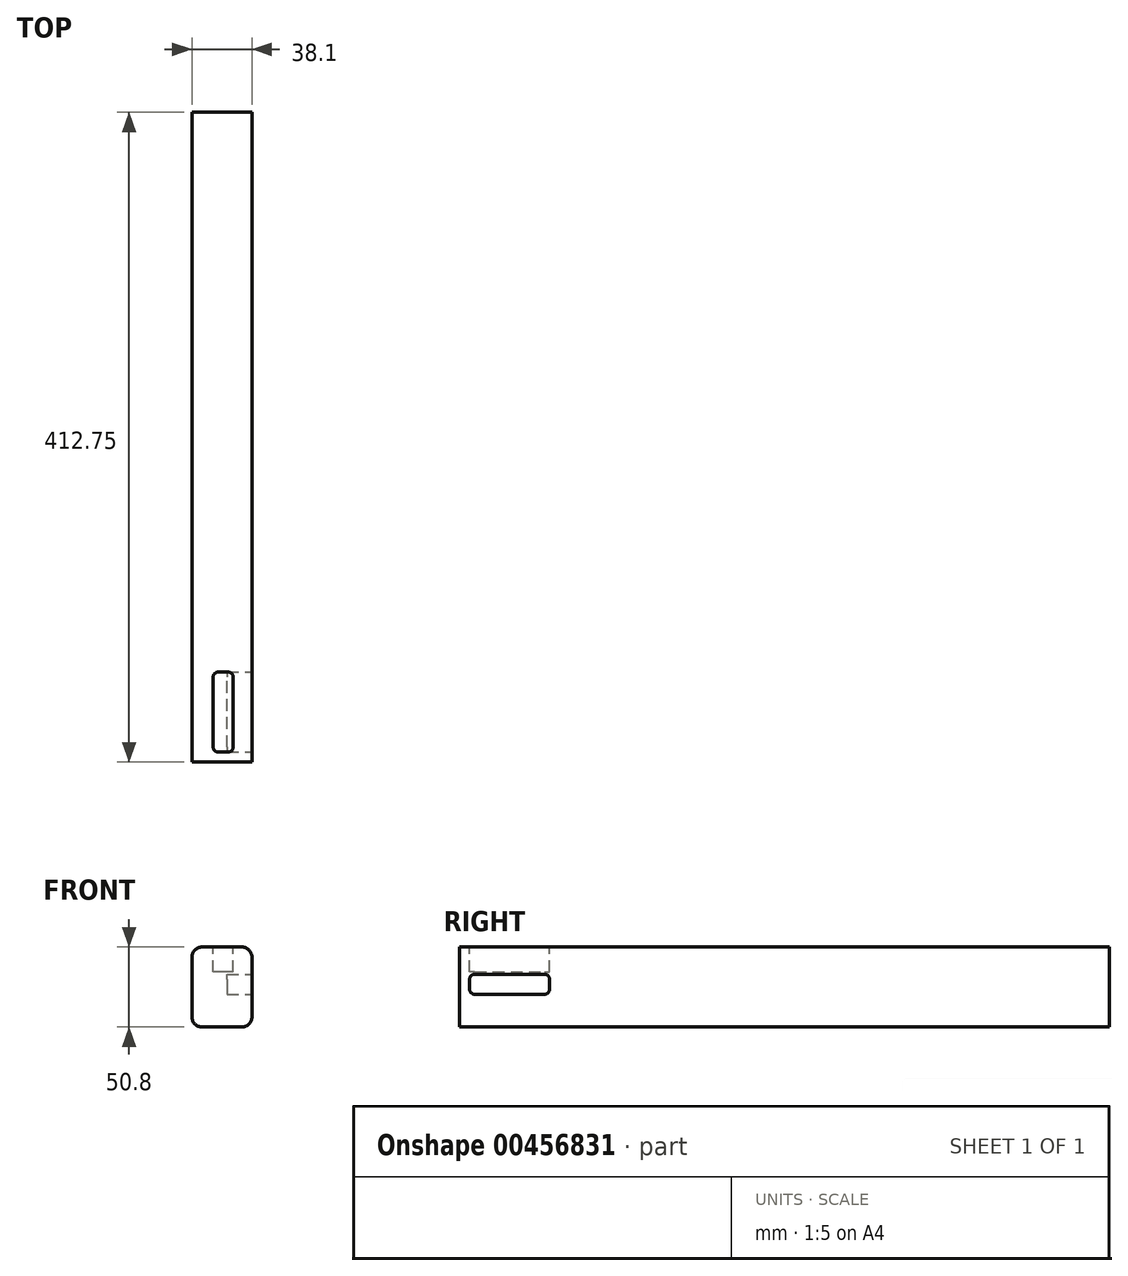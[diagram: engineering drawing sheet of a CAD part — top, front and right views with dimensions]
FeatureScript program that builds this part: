
annotation { "Feature Type Name" : "Feature", "Feature Type Description" : "" }
export const myFeature = defineFeature(function(context is Context, id is Id, definition is map)
    precondition{}
    {
        {
            var Q0;
            Q0=qCreatedBy(makeId("Front.planeOp"),FACE);
            var sketch = newSketch(context, id + "F0", { "sketchPlane" : qUnion([Q0])});
            skLineSegment(sketch, "E0", {"start": v(-21.46, 29.96) * mm, "end": v(16.64, 29.96) * mm});
            skLineSegment(sketch, "E1", {"start": v(16.64, 29.96) * mm, "end": v(16.64, -20.84) * mm});
            skLineSegment(sketch, "E2", {"start": v(16.64, -20.84) * mm, "end": v(-21.46, -20.84) * mm});
            skLineSegment(sketch, "E3", {"start": v(-21.46, -20.84) * mm, "end": v(-21.46, 29.96) * mm});
            skSolve(sketch);
        }
        {
            var Q0;
            Q0=qSketchRegion(id+"F0",true);
            extrude(context, id + "F1", {"entities" : qUnion([Q0]), "oppositeDirection" : true, "depth" : 412.75 * mm});
        }
        {
            var Q0;
            Q0=makeQuery(id+"F1.opExtrude","SWEPT_FACE",FACE,{"disambiguationData":[OSD([sQuery(id+"F0.wireOp",EDGE,"E1")])]});
            var sketch = newSketch(context, id + "F2", { "sketchPlane" : qUnion([Q0])});
            skLineSegment(sketch, "E4", {"start": v(9.52, 12.7) * mm, "end": v(53.98, 12.7) * mm});
            skLineSegment(sketch, "E5", {"start": v(57.15, 9.53) * mm, "end": v(57.15, 3.18) * mm});
            skLineSegment(sketch, "E6", {"start": v(53.98, 0) * mm, "end": v(9.52, 0) * mm});
            skLineSegment(sketch, "E7", {"start": v(6.35, 3.18) * mm, "end": v(6.35, 9.52) * mm});
            skPoint(sketch, "E8.visualSharp", {"position": v(57.15, 12.7) * mm});
            skArc(sketch, "E8.filletArc", {"start": v(57.15, 9.53) * mm, "mid": v(56.22, 11.77) * mm, "end": v(53.98, 12.7) * mm});
            skPoint(sketch, "E9.visualSharp", {"position": v(57.15, 0) * mm});
            skArc(sketch, "E9.filletArc", {"start": v(53.98, 0) * mm, "mid": v(56.22, 0.93) * mm, "end": v(57.15, 3.18) * mm});
            skPoint(sketch, "E10.visualSharp", {"position": v(6.35, 12.7) * mm});
            skArc(sketch, "E10.filletArc", {"start": v(9.52, 12.7) * mm, "mid": v(7.28, 11.77) * mm, "end": v(6.35, 9.52) * mm});
            skPoint(sketch, "E11.visualSharp", {"position": v(6.35, 0) * mm});
            skArc(sketch, "E11.filletArc", {"start": v(6.35, 3.18) * mm, "mid": v(7.28, 0.93) * mm, "end": v(9.52, 0) * mm});
            skSolve(sketch);
        }
        {
            var Q0;
            Q0=qSketchRegion(id+"F2",true);
            extrude(context, id + "F3", {"entities" : qUnion([Q0]), "operationType" : NewBodyOperationType.REMOVE, "oppositeDirection" : true, "depth" : 15.88 * mm});
        }
        {
            var Q0;
            Q0=makeQuery(id+"F1.opExtrude","SWEPT_FACE",FACE,{"disambiguationData":[OSD([sQuery(id+"F0.wireOp",EDGE,"E0")])]});
            var sketch = newSketch(context, id + "F4", { "sketchPlane" : qUnion([Q0])});
            skLineSegment(sketch, "E12", {"start": v(-7.97, 53.98) * mm, "end": v(-7.97, 9.52) * mm});
            skLineSegment(sketch, "E13", {"start": v(-4.8, 6.35) * mm, "end": v(1.55, 6.35) * mm});
            skLineSegment(sketch, "E14", {"start": v(4.73, 9.53) * mm, "end": v(4.73, 53.98) * mm});
            skLineSegment(sketch, "E15", {"start": v(1.55, 57.15) * mm, "end": v(-4.8, 57.15) * mm});
            skPoint(sketch, "E16.visualSharp", {"position": v(-7.97, 57.15) * mm});
            skArc(sketch, "E16.filletArc", {"start": v(-4.8, 57.15) * mm, "mid": v(-7.04, 56.22) * mm, "end": v(-7.97, 53.98) * mm});
            skPoint(sketch, "E17.visualSharp", {"position": v(4.73, 57.15) * mm});
            skArc(sketch, "E17.filletArc", {"start": v(4.73, 53.98) * mm, "mid": v(3.8, 56.22) * mm, "end": v(1.55, 57.15) * mm});
            skPoint(sketch, "E18.visualSharp", {"position": v(4.73, 6.35) * mm});
            skArc(sketch, "E18.filletArc", {"start": v(1.55, 6.35) * mm, "mid": v(3.8, 7.28) * mm, "end": v(4.73, 9.53) * mm});
            skPoint(sketch, "E19.visualSharp", {"position": v(-7.97, 6.35) * mm});
            skArc(sketch, "E19.filletArc", {"start": v(-7.97, 9.52) * mm, "mid": v(-7.04, 7.28) * mm, "end": v(-4.8, 6.35) * mm});
            skSolve(sketch);
        }
        {
            var Q0;
            Q0=qSketchRegion(id+"F4",true);
            extrude(context, id + "F5", {"entities" : qUnion([Q0]), "operationType" : NewBodyOperationType.REMOVE, "oppositeDirection" : true, "depth" : 15.88 * mm});
        }
        {
            var Q0;
            Q0=makeQuery(id+"F1.opExtrude","SWEPT_EDGE",EDGE,{"disambiguationData":[OSD([sQuery(id+"F0.wireOp",EDGE,"E1"),sQuery(id+"F0.wireOp",EDGE,"E2")])]});
            var Q1;
            Q1=makeQuery(id+"F1.opExtrude","SWEPT_EDGE",EDGE,{"disambiguationData":[OSD([sQuery(id+"F0.wireOp",EDGE,"E2"),sQuery(id+"F0.wireOp",EDGE,"E3")])]});
            var Q2;
            Q2=makeQuery(id+"F1.opExtrude","SWEPT_EDGE",EDGE,{"disambiguationData":[OSD([sQuery(id+"F0.wireOp",EDGE,"E0"),sQuery(id+"F0.wireOp",EDGE,"E1")])]});
            var Q3;
            Q3=makeQuery(id+"F1.opExtrude","SWEPT_EDGE",EDGE,{"disambiguationData":[OSD([sQuery(id+"F0.wireOp",EDGE,"E0"),sQuery(id+"F0.wireOp",EDGE,"E3")])]});
            fillet(context, id + "F6", {"entities" : qUnion([Q0, Q1, Q2, Q3]), "radius" : 6.35 * mm, "tangentPropagation" : true, "allowEdgeOverflow" : false});
        }
    });
